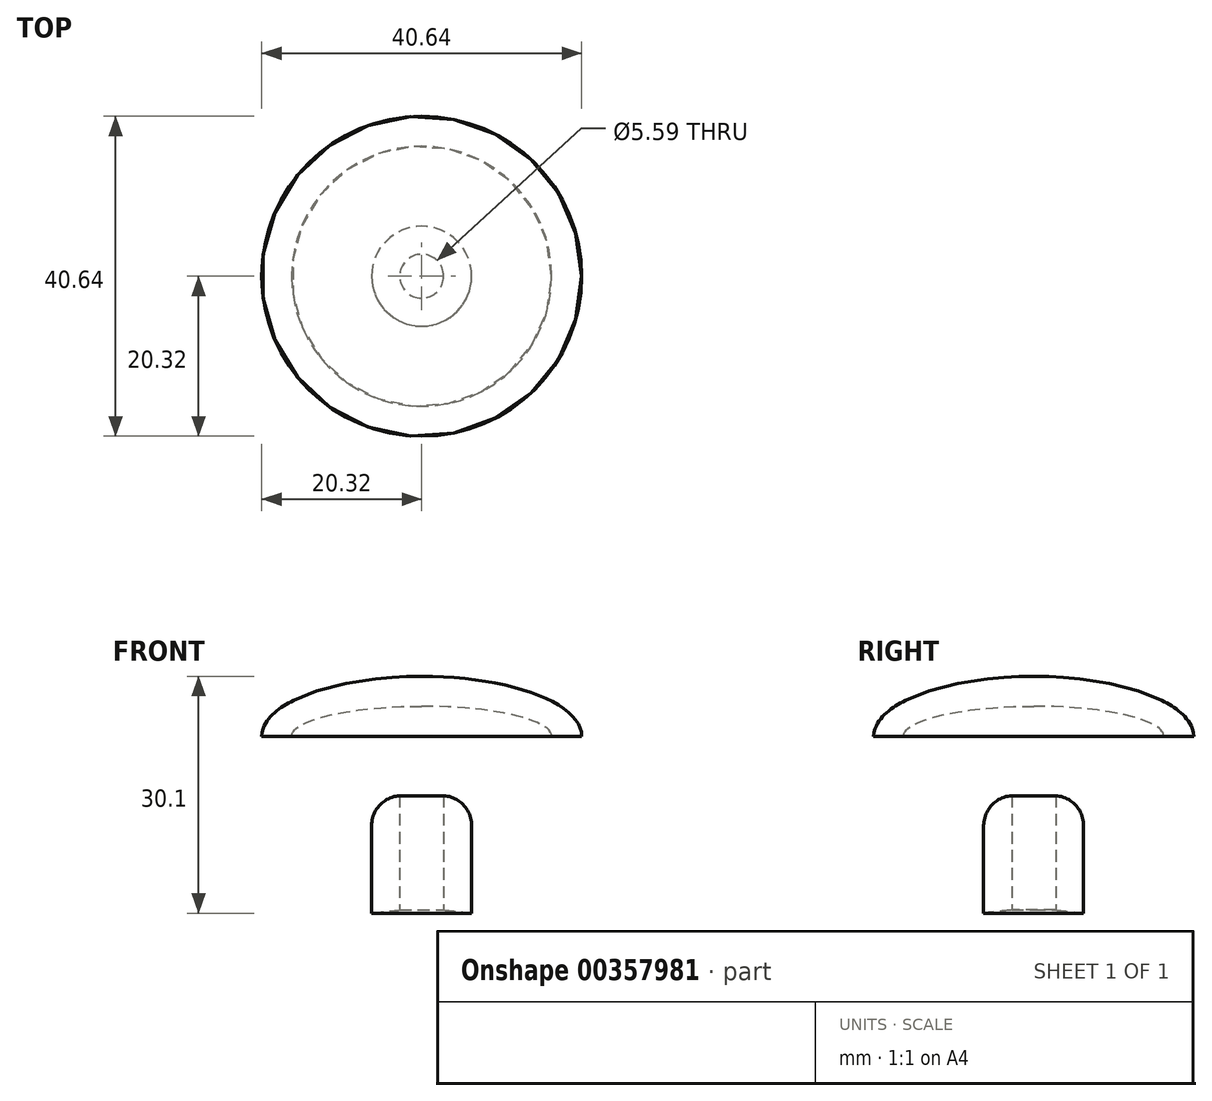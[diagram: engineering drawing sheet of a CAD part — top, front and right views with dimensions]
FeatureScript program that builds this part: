
annotation { "Feature Type Name" : "Feature", "Feature Type Description" : "" }
export const myFeature = defineFeature(function(context is Context, id is Id, definition is map)
    precondition{}
    {
        {
            var Q0;
            Q0=qCreatedBy(makeId("Front.planeOp"),FACE);
            var sketch = newSketch(context, id + "F0", { "sketchPlane" : qUnion([Q0])});
            skEllipticalArc(sketch, "E0", {});
            skLineSegment(sketch, "E1", {"start": v(6.35, -7.24) * mm, "end": v(6.35, -22.48) * mm});
            skArc(sketch, "E2", {"start": v(6.35, -22.48) * mm, "mid": v(3.18, -22.12) * mm, "end": v(0, -21.84) * mm});
            skLineSegment(sketch, "E3", {"start": v(0, 7.62) * mm, "end": v(0, -21.84) * mm});
            skPoint(sketch, "E4.orphan", {"position": v(-23.9, -22.48) * mm});
            skLineSegment(sketch, "E5", {"start": v(0, -7.62) * mm, "end": v(0, -3.81) * mm});
            skLineSegment(sketch, "E6", {"start": v(20.32, 0) * mm, "end": v(16.51, 0) * mm});
            skPoint(sketch, "E6.endSnap0", {"position": v(20.32, 0) * mm});
            skEllipse(sketch, "E7", {"center": v(0, 0) * mm, "majorRadius": 16.51 * mm, "minorRadius": 3.81 * mm, "majorAxis": v(1, 0)});
            skLineSegment(sketch, "E8", {"start": v(2.8, -7.55) * mm, "end": v(2.8, -22.08) * mm});
            skLineSegment(sketch, "E9", {"start": v(0, 3.81) * mm, "end": v(0, -3.81) * mm});
            skLineSegment(sketch, "E10", {"start": v(0, 3.81) * mm, "end": v(0, 7.62) * mm});
            const initialGuessF0  = {"E0": [0, 0, 1, 0, 0.02032, 0.00762, 4.71238898038469, 1.5707963267948966]};
            skSetInitialGuess(sketch, initialGuessF0);
            skSolve(sketch);
        }
        {
            var Q0;
            {var subQ0=sQuery(id+"F0.wireOp",EDGE,"E6");Q0=makeQuery(id+"F0.imprint","IMPRINT",FACE,{"disambiguationData":[TD([[makeQuery(id+"F0.imprint","IMPRINT",EDGE,{"derivedFrom":subQ0}),-1.0]])]});}
            var Q1;
            {var subQ2=sQuery(id+"F0.wireOp",EDGE,"E9");Q1=makeQuery(id+"F0.imprint","IMPRINT",FACE,{"disambiguationData":[TD([[makeQuery(id+"F0.imprint","IMPRINT",EDGE,{"derivedFrom":subQ2}),1.0]])]});}
            var Q2;
            {var subQ0=sQuery(id+"F0.wireOp",EDGE,"E5");Q2=makeQuery(id+"F0.imprint","IMPRINT",FACE,{"disambiguationData":[TD([[makeQuery(id+"F0.imprint","IMPRINT",EDGE,{"derivedFrom":subQ0}),-1.0]])]});}
            var Q3;
            {var subQ0=sQuery(id+"F0.wireOp",EDGE,"E1");Q3=makeQuery(id+"F0.imprint","IMPRINT",FACE,{"disambiguationData":[TD([[makeQuery(id+"F0.imprint","IMPRINT",EDGE,{"derivedFrom":subQ0}),-1.0]])]});}
            var Q4;
            Q4=sQuery(id+"F0.wireOp",EDGE,"E3");
            revolve(context, id + "F1", {"entities" : qUnion([Q0, Q1, Q2, Q3]), "axis" : qUnion([Q4]), "revolveType" : RevolveType.FULL, "oppositeDirection" : true});
        }
        {
            var Q0;
            Q0=makeQuery(id+"F1.opRevolve","SWEPT_EDGE",EDGE,{"disambiguationData":[OSD([sQuery(id+"F0.wireOp",EDGE,"E0"),sQuery(id+"F0.wireOp",EDGE,"E1")])]});
            fillet(context, id + "F2", {"entities" : qUnion([Q0]), "radius" : 3.8 * mm, "tangentPropagation" : true, "allowEdgeOverflow" : false});
        }
    });
